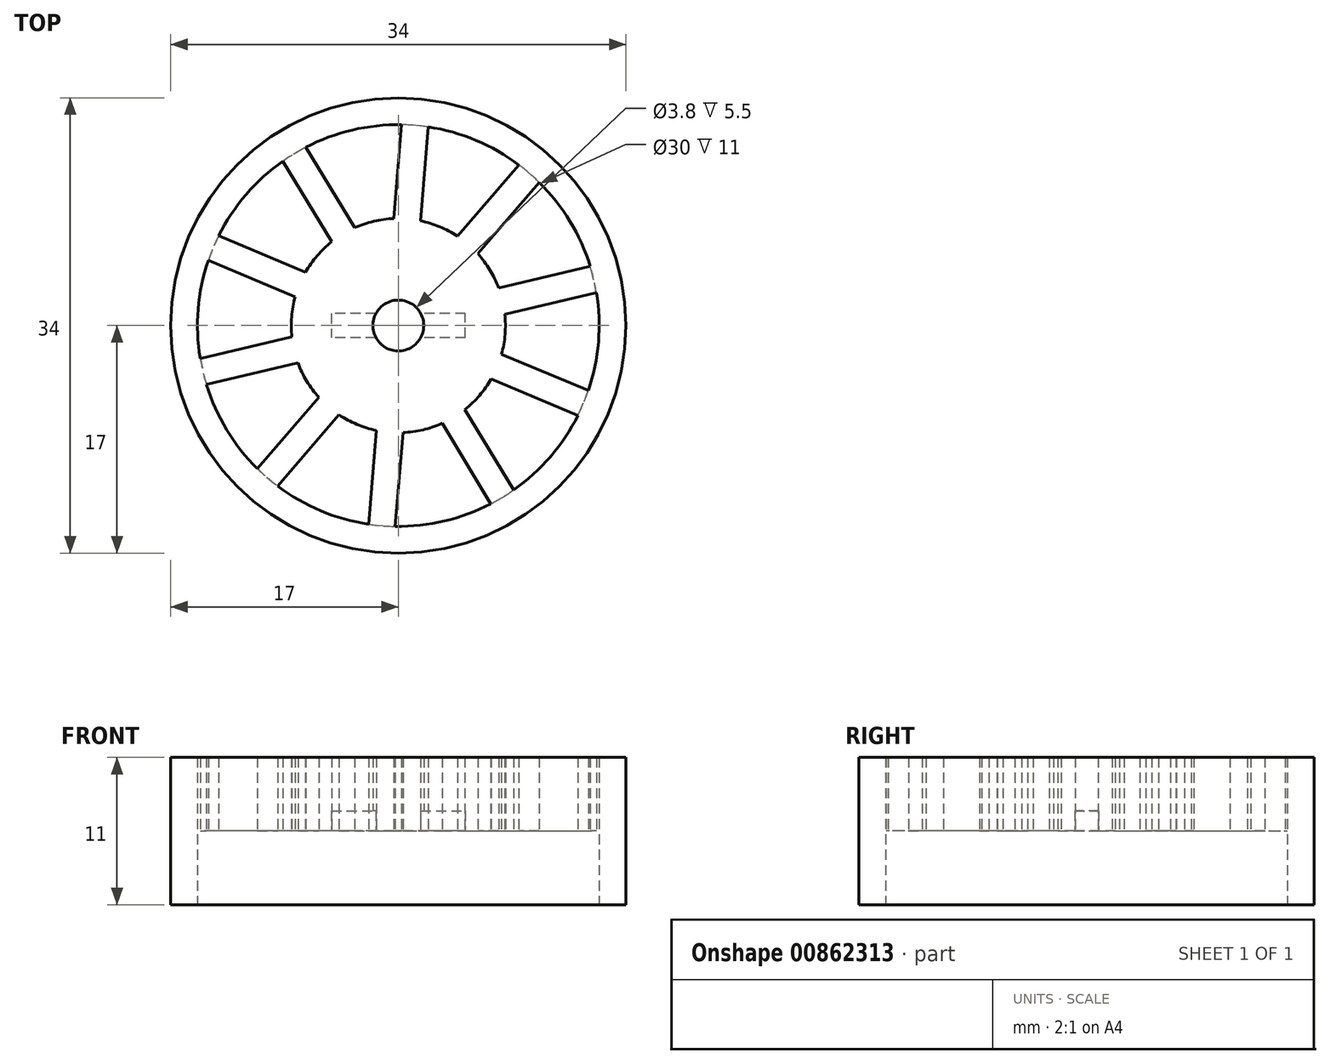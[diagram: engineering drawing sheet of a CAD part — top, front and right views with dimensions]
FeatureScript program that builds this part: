
annotation { "Feature Type Name" : "Feature", "Feature Type Description" : "" }
export const myFeature = defineFeature(function(context is Context, id is Id, definition is map)
    precondition{}
    {
        {
            var Q0;
            Q0=qCreatedBy(makeId("Top.planeOp"),FACE);
            var sketch = newSketch(context, id + "F0", { "sketchPlane" : qUnion([Q0])});
            skArc(sketch, "E0", {"start": v(-4.42, -6.67) * mm, "mid": v(-3.09, -7.38) * mm, "end": v(-1.65, -7.83) * mm});
            skArc(sketch, "E1", {"start": v(-14.34, -4.41) * mm, "mid": v(-12.82, -7.79) * mm, "end": v(-10.52, -10.7) * mm});
            skCircle(sketch, "E2", {"center": v(0, 0) * mm, "radius": 17 * mm});
            skLineSegment(sketch, "E3.0", {"start": v(-3.27, 7.3) * mm, "end": v(-6.92, 13.31) * mm});
            skLineSegment(sketch, "E4.0", {"start": v(-4.98, 6.26) * mm, "end": v(-8.63, 12.27) * mm});
            skLineSegment(sketch, "E5.1.0", {"start": v(-6.94, 3.99) * mm, "end": v(-13.42, 6.7) * mm});
            skLineSegment(sketch, "E5.1.1", {"start": v(-7.7, 2.14) * mm, "end": v(-14.2, 4.86) * mm});
            skLineSegment(sketch, "E5.2.0", {"start": v(-7.95, -0.85) * mm, "end": v(-14.8, -2.46) * mm});
            skLineSegment(sketch, "E5.2.1", {"start": v(-7.5, -2.8) * mm, "end": v(-14.34, -4.41) * mm});
            skLineSegment(sketch, "E5.3.0", {"start": v(-5.94, -5.36) * mm, "end": v(-10.52, -10.7) * mm});
            skLineSegment(sketch, "E5.3.1", {"start": v(-4.42, -6.67) * mm, "end": v(-9, -12) * mm});
            skLineSegment(sketch, "E5.4.0", {"start": v(-1.65, -7.83) * mm, "end": v(-2.23, -14.83) * mm});
            skLineSegment(sketch, "E5.4.1", {"start": v(0.34, -8) * mm, "end": v(-0.23, -15) * mm});
            skLineSegment(sketch, "E5.5.0", {"start": v(3.27, -7.3) * mm, "end": v(6.92, -13.31) * mm});
            skLineSegment(sketch, "E5.5.1", {"start": v(4.98, -6.26) * mm, "end": v(8.63, -12.27) * mm});
            skLineSegment(sketch, "E5.6.0", {"start": v(6.94, -3.99) * mm, "end": v(13.42, -6.7) * mm});
            skLineSegment(sketch, "E5.6.1", {"start": v(7.7, -2.14) * mm, "end": v(14.2, -4.86) * mm});
            skLineSegment(sketch, "E5.7.0", {"start": v(7.95, 0.85) * mm, "end": v(14.8, 2.46) * mm});
            skLineSegment(sketch, "E5.7.1", {"start": v(7.5, 2.8) * mm, "end": v(14.34, 4.41) * mm});
            skLineSegment(sketch, "E5.8.0", {"start": v(5.94, 5.36) * mm, "end": v(10.52, 10.7) * mm});
            skLineSegment(sketch, "E5.8.1", {"start": v(4.42, 6.67) * mm, "end": v(9, 12) * mm});
            skLineSegment(sketch, "E5.9.0", {"start": v(1.65, 7.83) * mm, "end": v(2.23, 14.83) * mm});
            skLineSegment(sketch, "E5.9.1", {"start": v(-0.34, 8) * mm, "end": v(0.23, 15) * mm});
            skArc(sketch, "E6.trimOffspring", {"start": v(-8.63, 12.27) * mm, "mid": v(-11.37, 9.79) * mm, "end": v(-13.42, 6.7) * mm});
            skArc(sketch, "E7.trimOffspring", {"start": v(-14.2, 4.86) * mm, "mid": v(-14.95, 1.23) * mm, "end": v(-14.8, -2.46) * mm});
            skArc(sketch, "E8.trimOffspring", {"start": v(0.23, 15) * mm, "mid": v(-3.45, 14.6) * mm, "end": v(-6.92, 13.31) * mm});
            skArc(sketch, "E9.trimOffspring", {"start": v(9, 12) * mm, "mid": v(5.8, 13.84) * mm, "end": v(2.23, 14.83) * mm});
            skArc(sketch, "E10.trimOffspring", {"start": v(14.34, 4.41) * mm, "mid": v(12.82, 7.79) * mm, "end": v(10.52, 10.7) * mm});
            skArc(sketch, "E11.trimOffspring", {"start": v(-0.23, -15) * mm, "mid": v(3.45, -14.6) * mm, "end": v(6.92, -13.31) * mm});
            skArc(sketch, "E12.trimOffspring", {"start": v(-9, -12) * mm, "mid": v(-5.8, -13.84) * mm, "end": v(-2.23, -14.83) * mm});
            skArc(sketch, "E13.trimOffspring", {"start": v(8.63, -12.27) * mm, "mid": v(11.37, -9.79) * mm, "end": v(13.42, -6.7) * mm});
            skArc(sketch, "E14.trimOffspring", {"start": v(14.2, -4.86) * mm, "mid": v(14.95, -1.23) * mm, "end": v(14.8, 2.46) * mm});
            skArc(sketch, "E15.trimOffspring", {"start": v(0.34, -8) * mm, "mid": v(1.84, -7.79) * mm, "end": v(3.27, -7.3) * mm});
            skArc(sketch, "E16.trimOffspring", {"start": v(4.98, -6.26) * mm, "mid": v(6.06, -5.22) * mm, "end": v(6.94, -3.99) * mm});
            skArc(sketch, "E17.trimOffspring", {"start": v(7.7, -2.14) * mm, "mid": v(7.97, -0.66) * mm, "end": v(7.95, 0.85) * mm});
            skArc(sketch, "E18.trimOffspring", {"start": v(7.5, 2.8) * mm, "mid": v(6.84, 4.15) * mm, "end": v(5.94, 5.36) * mm});
            skArc(sketch, "E19.trimOffspring", {"start": v(4.42, 6.67) * mm, "mid": v(3.09, 7.38) * mm, "end": v(1.65, 7.83) * mm});
            skArc(sketch, "E20.trimOffspring", {"start": v(-0.34, 8) * mm, "mid": v(-1.84, 7.79) * mm, "end": v(-3.27, 7.3) * mm});
            skArc(sketch, "E21.trimOffspring", {"start": v(-4.98, 6.26) * mm, "mid": v(-6.06, 5.22) * mm, "end": v(-6.94, 3.99) * mm});
            skArc(sketch, "E22.trimOffspring", {"start": v(-7.7, 2.14) * mm, "mid": v(-7.97, 0.66) * mm, "end": v(-7.95, -0.85) * mm});
            skCircle(sketch, "E23", {"center": v(0, 0) * mm, "radius": 1.9 * mm});
            skArc(sketch, "E24.trimOffspring", {"start": v(-7.5, -2.8) * mm, "mid": v(-6.84, -4.15) * mm, "end": v(-5.94, -5.36) * mm});
            skSolve(sketch);
        }
        {
            var Q0;
            Q0=qSketchRegion(id+"F0",true);
            extrude(context, id + "F1", {"entities" : qUnion([Q0]), "depth" : 11 * mm, "offsetDistance" : 25 * mm});
        }
        {
            var Q0;
            Q0=qCreatedBy(makeId("Top.planeOp"),FACE);
            var sketch = newSketch(context, id + "F2", { "sketchPlane" : qUnion([Q0])});
            skCircle(sketch, "E25", {"center": v(0, 0) * mm, "radius": 15 * mm});
            skSolve(sketch);
        }
        {
            var Q0;
            Q0=qSketchRegion(id+"F2",true);
            extrude(context, id + "F3", {"entities" : qUnion([Q0]), "operationType" : NewBodyOperationType.REMOVE, "depth" : 5.5 * mm, "offsetDistance" : 25 * mm});
        }
        {
            var Q0;
            Q0=qCreatedBy(makeId("Top.planeOp"),FACE);
            cPlane(context, id + "F4", {"entities" : qUnion([Q0]), "cplaneType" : CPlaneType.OFFSET, "offset" : 5 * mm, "width" : 150 * mm, "height" : 150 * mm});
        }
        {
            var Q0;
            Q0=qCreatedBy(id+"F4.planeOp",FACE);
            var sketch = newSketch(context, id + "F5", { "sketchPlane" : qUnion([Q0])});
            skLineSegment(sketch, "E26", {"start": v(0, 0) * mm, "end": v(-5, 0) * mm});
            skLineSegment(sketch, "E27", {"start": v(-5, 0) * mm, "end": v(-5, 0.9) * mm});
            skLineSegment(sketch, "E28", {"start": v(0, 0) * mm, "end": v(0, 3.2) * mm});
            skLineSegment(sketch, "E29", {"start": v(-5, 0.9) * mm, "end": v(0, 0.9) * mm});
            skLineSegment(sketch, "E30.MirrorCS", {"start": v(5, 0.9) * mm, "end": v(0, 0.9) * mm});
            skLineSegment(sketch, "E31.MirrorCS", {"start": v(5, 0) * mm, "end": v(5, 0.9) * mm});
            skLineSegment(sketch, "E32.MirrorCS", {"start": v(-5, -0.9) * mm, "end": v(0, -0.9) * mm});
            skLineSegment(sketch, "E33.MirrorCS", {"start": v(-5, 0) * mm, "end": v(-5, -0.9) * mm});
            skLineSegment(sketch, "E34.MirrorCS", {"start": v(5, -0.9) * mm, "end": v(0, -0.9) * mm});
            skLineSegment(sketch, "E35.MirrorCS", {"start": v(5, 0) * mm, "end": v(5, -0.9) * mm});
            skSolve(sketch);
        }
        {
            var Q0;
            Q0 = qSketchRegion(id + "F5", true);
            extrude(context, id + "F6", {"entities" : qUnion([Q0]), "operationType" : NewBodyOperationType.REMOVE, "depth" : 2 * mm, "offsetDistance" : 25 * mm});
        }
    });
